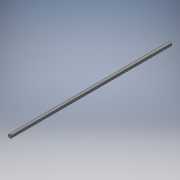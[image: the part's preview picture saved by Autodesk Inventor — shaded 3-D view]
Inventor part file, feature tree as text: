
AUTODESK INVENTOR PART (.ipt)
format: ipt  version: 2018 (Build 220112000, 112)  size: 97,280 bytes
history: native  units: in
note: dims shown in document units (in); Inventor stores cm internally (conversion verified against a paired STEP export)
features: extrude x1, sketch x1
ambient origin geometry x8: Origin, YZ Plane, XZ Plane, XY Plane, X Axis, Y Axis, Z Axis, Center Point
bodies: Solid1 (feature_tree)
feature tree (2):
  extrude  "Extrusion1"  Depth=0.5in
  sketch  "Sketch1"  dims[d1=14.0in d2=0.0in d3=0.5in]
